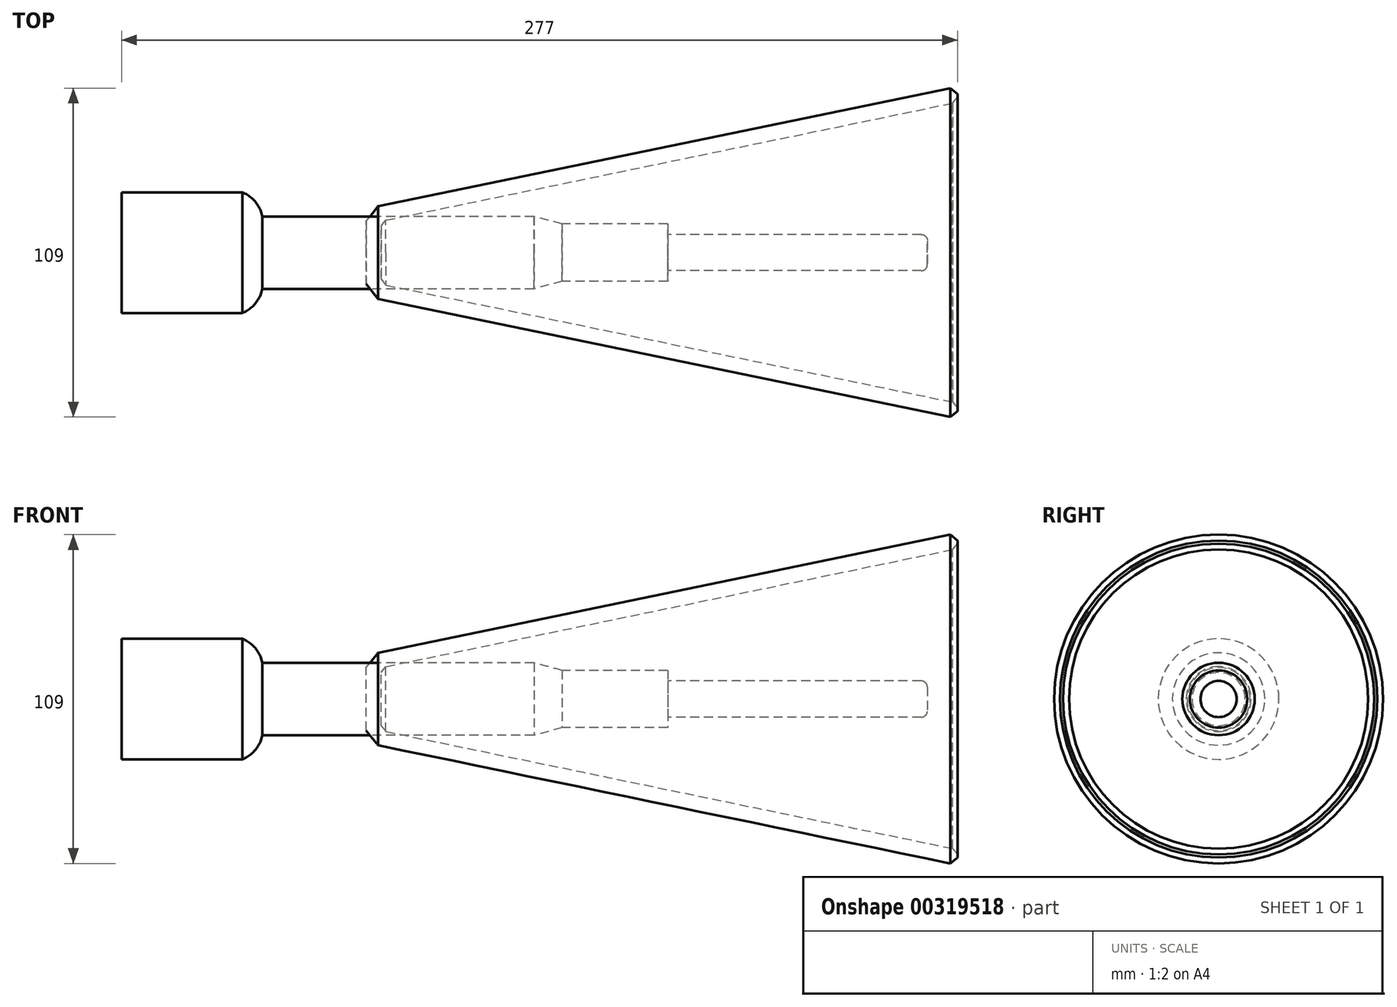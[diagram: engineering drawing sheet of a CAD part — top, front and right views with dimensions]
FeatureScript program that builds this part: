
annotation { "Feature Type Name" : "Feature", "Feature Type Description" : "" }
export const myFeature = defineFeature(function(context is Context, id is Id, definition is map)
    precondition{}
    {
        {
            var Q0;
            Q0=qCreatedBy(makeId("Front.planeOp"),FACE);
            var sketch = newSketch(context, id + "F0", { "sketchPlane" : qUnion([Q0])});
            skLineSegment(sketch, "E0", {"start": v(0, 0) * mm, "end": v(267, 0) * mm, "construction": true});
            skLineSegment(sketch, "E1", {"start": v(267, 0) * mm, "end": v(267, 6) * mm});
            skLineSegment(sketch, "E2", {"start": v(267, 6) * mm, "end": v(181, 6) * mm});
            skLineSegment(sketch, "E3", {"start": v(181, 6) * mm, "end": v(181, 9.5) * mm});
            skLineSegment(sketch, "E4", {"start": v(181, 9.5) * mm, "end": v(146, 9.5) * mm});
            skLineSegment(sketch, "E5", {"start": v(0, 0) * mm, "end": v(0, 20) * mm});
            skLineSegment(sketch, "E6", {"start": v(0, 20) * mm, "end": v(40, 20) * mm});
            skLineSegment(sketch, "E7", {"start": v(146, 9.5) * mm, "end": v(136.67, 12) * mm});
            skLineSegment(sketch, "E8", {"start": v(136.67, 12) * mm, "end": v(46.67, 12) * mm});
            skArc(sketch, "E9", {"start": v(46.67, 12) * mm, "mid": v(44.34, 16.84) * mm, "end": v(40, 20) * mm});
            skLineSegment(sketch, "E10", {"start": v(0, 0) * mm, "end": v(267, 0) * mm});
            skSolve(sketch);
        }
        {
            var Q0;
            Q0=makeQuery(id+"F0.imprint","IMPRINT",FACE,{"disambiguationData":[TD([[makeQuery(id+"F0.imprint","IMPRINT",EDGE,{"derivedFrom":sQuery(id+"F0.wireOp",EDGE,"E1")}),1.0]])]});
            var Q1;
            Q1=sQuery(id+"F0.wireOp",EDGE,"E10");
            revolve(context, id + "F1", {"entities" : qUnion([Q0]), "axis" : qUnion([Q1]), "revolveType" : RevolveType.FULL});
        }
        {
            var Q0;
            Q0=makeQuery(id+"F1.opRevolve","SWEPT_EDGE",EDGE,{"disambiguationData":[OSD([sQuery(id+"F0.wireOp",EDGE,"E1"),sQuery(id+"F0.wireOp",EDGE,"E2")])]});
            fillet(context, id + "F2", {"entities" : qUnion([Q0]), "radius" : 2 * mm, "tangentPropagation" : true, "allowEdgeOverflow" : false});
        }
        {
            var Q0;
            Q0=makeQuery(id+"F1.opRevolve","SWEPT_FACE",FACE,{"disambiguationData":[OSD([sQuery(id+"F0.wireOp",EDGE,"E3")])]});
            cPlane(context, id + "F3", {"entities" : qUnion([Q0]), "cplaneType" : CPlaneType.OFFSET, "offset" : 100 * mm, "oppositeDirection" : true, "width" : 150 * mm, "height" : 150 * mm});
        }
        {
            var Q0;
            Q0=qCreatedBy(id+"F3.planeOp",FACE);
            var sketch = newSketch(context, id + "F4", { "sketchPlane" : qUnion([Q0])});
            skCircle(sketch, "E11.0", {"center": v(0, 0) * mm, "radius": 12 * mm, "construction": true});
            skCircle(sketch, "E12.0", {"center": v(0, 0) * mm, "radius": 4 * mm, "construction": true});
            skCircle(sketch, "E13", {"center": v(0, 0) * mm, "radius": 14.5 * mm});
            skSolve(sketch);
        }
        {
            var Q0;
            Q0=makeQuery(id+"F1.opRevolve","SWEPT_FACE",FACE,{"disambiguationData":[OSD([sQuery(id+"F0.wireOp",EDGE,"E1")])]});
            cPlane(context, id + "F5", {"entities" : qUnion([Q0]), "cplaneType" : CPlaneType.OFFSET, "offset" : 10 * mm, "width" : 150 * mm, "height" : 150 * mm});
        }
        {
            var Q0;
            Q0=qCreatedBy(id+"F5.planeOp",FACE);
            var sketch = newSketch(context, id + "F6", { "sketchPlane" : qUnion([Q0])});
            skCircle(sketch, "E14.0", {"center": v(0, 0) * mm, "radius": 4 * mm, "construction": true});
            skCircle(sketch, "E15", {"center": v(0, 0) * mm, "radius": 55 * mm});
            skSolve(sketch);
        }
        {
            var Q1;
            Q1=makeQuery(id+"F4.imprint","IMPRINT",FACE,{"disambiguationData":[TD([[makeQuery(id+"F4.imprint","IMPRINT",EDGE,{"derivedFrom":sQuery(id+"F4.wireOp",EDGE,"E13")}),1.0]])]});
            var Q2;
            Q2=makeQuery(id+"F6.imprint","IMPRINT",FACE,{"disambiguationData":[TD([[makeQuery(id+"F6.imprint","IMPRINT",EDGE,{"derivedFrom":sQuery(id+"F6.wireOp",EDGE,"E15")}),1.0]])]});
            loft(context, id + "F7", {"sheetProfilesArray" : [{ "sheetProfileEntities" : qUnion([Q1]) }, { "sheetProfileEntities" : qUnion([Q2]) }]});
        }
        {
            var Q0;
            Q0=makeQuery(id+"F7.opLoft","CAP_FACE",FACE,{"disambiguationData":[OSD([makeQuery(id+"F6.imprint","IMPRINT",FACE,{"disambiguationData":[TD([[makeQuery(id+"F6.imprint","IMPRINT",EDGE,{"derivedFrom":sQuery(id+"F6.wireOp",EDGE,"E15")}),1.0]])]})])],"isStart":true});
            shell(context, id + "F8", {"entities" : qUnion([Q0]), "thickness" : 5 * mm});
        }
        {
            var Q0;
            Q0=makeQuery(id+"F8.opShell","OFFSET_EDGE",EDGE,{"disambiguationData":[OSD([sQuery(id+"F4.wireOp",EDGE,"E13"),sQuery(id+"F6.wireOp",EDGE,"E15")])]});
            var Q1;
            Q1=makeQuery(id+"F7.opLoft","MID_CAP_EDGE",EDGE,{"disambiguationData":[OSD([sQuery(id+"F4.wireOp",EDGE,"E13"),sQuery(id+"F6.wireOp",EDGE,"E15")])],"capPos":1.0});
            chamfer(context, id + "F9", {"entities" : qUnion([Q0, Q1]), "width" : 2 * mm, "tangentPropagation" : true});
        }
        {
            var Q0;
            Q0=makeQuery(id+"F7.opLoft","MID_CAP_EDGE",EDGE,{"disambiguationData":[OSD([sQuery(id+"F4.wireOp",EDGE,"E13")])],"capPos":0.0});
            chamfer(context, id + "F10", {"entities" : qUnion([Q0]), "width" : 5 * mm, "tangentPropagation" : true});
        }
    });
